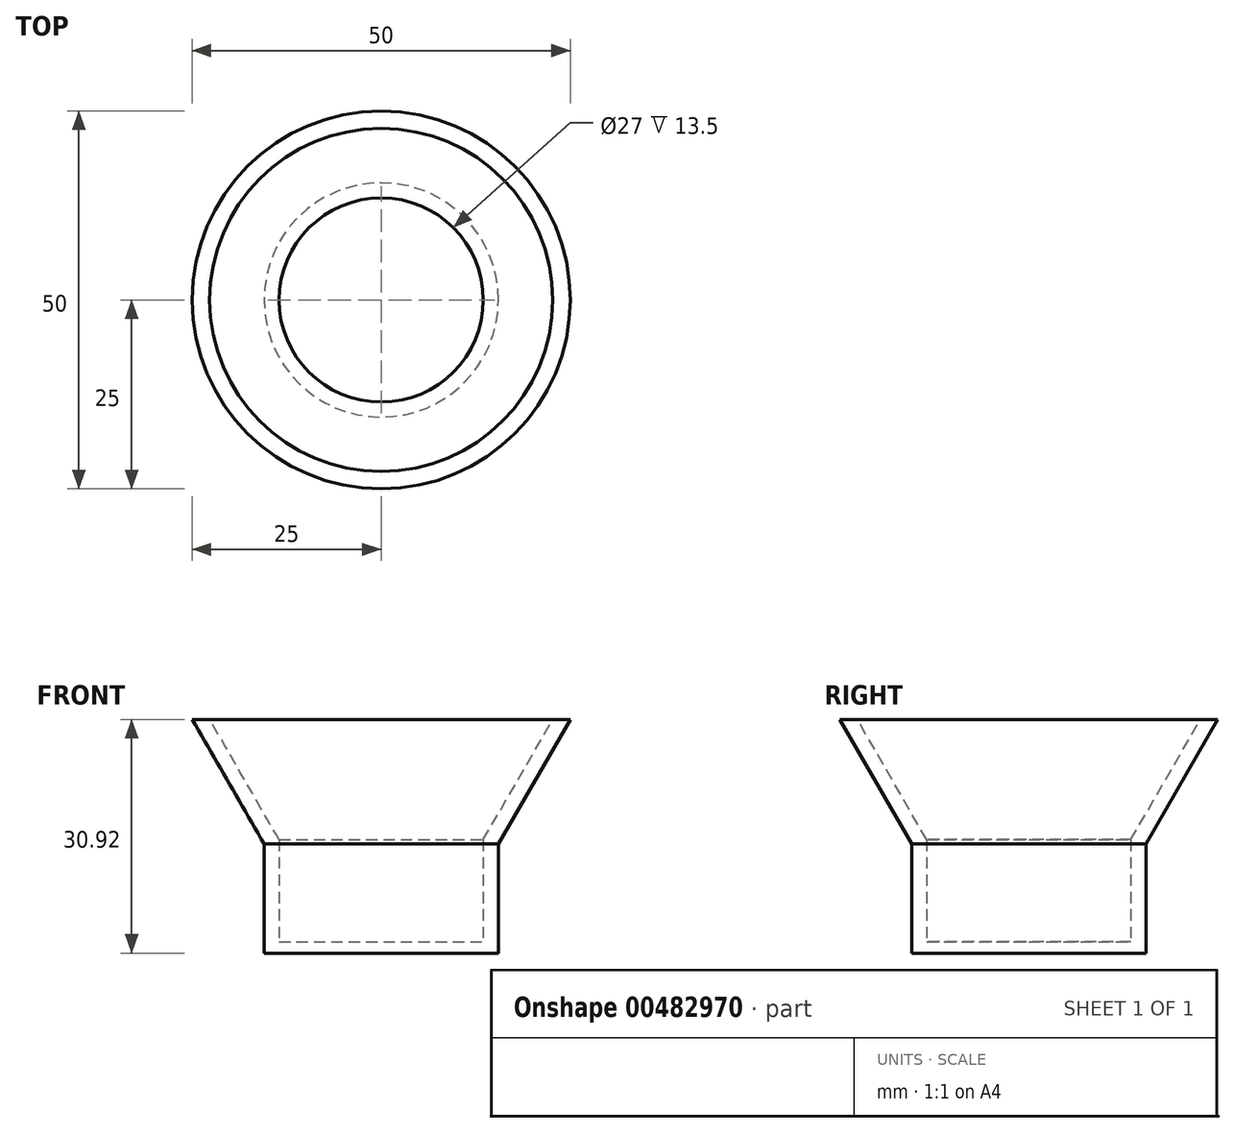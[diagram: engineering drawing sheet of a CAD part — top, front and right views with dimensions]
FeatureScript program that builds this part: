
annotation { "Feature Type Name" : "Feature", "Feature Type Description" : "" }
export const myFeature = defineFeature(function(context is Context, id is Id, definition is map)
    precondition{}
    {
        {
            var Q0;
            Q0=qCreatedBy(makeId("Front.planeOp"),FACE);
            var sketch = newSketch(context, id + "F0", { "sketchPlane" : qUnion([Q0])});
            skLineSegment(sketch, "E0", {"start": v(0, 0) * mm, "end": v(0, 42.36) * mm, "construction": true});
            skLineSegment(sketch, "E1", {"start": v(13.5, 0) * mm, "end": v(13.5, 15) * mm});
            skLineSegment(sketch, "E2", {"start": v(13.5, 15) * mm, "end": v(22.7, 30.92) * mm});
            skLineSegment(sketch, "E3", {"start": v(22.7, 30.92) * mm, "end": v(25, 30.92) * mm});
            skLineSegment(sketch, "E4", {"start": v(25, 30.92) * mm, "end": v(15.5, 14.46) * mm});
            skLineSegment(sketch, "E5", {"start": v(15.5, 14.46) * mm, "end": v(15.5, 0) * mm});
            skLineSegment(sketch, "E6", {"start": v(15.5, 0) * mm, "end": v(13.5, 0) * mm});
            skLineSegment(sketch, "E7.MirrorCS", {"start": v(-22.7, 30.92) * mm, "end": v(-25, 30.92) * mm});
            skLineSegment(sketch, "E8.MirrorCS", {"start": v(-15.5, 0) * mm, "end": v(-13.5, 0) * mm});
            skLineSegment(sketch, "E9.MirrorCS", {"start": v(-13.5, 15) * mm, "end": v(-22.7, 30.92) * mm});
            skLineSegment(sketch, "E10.MirrorCS", {"start": v(-25, 30.92) * mm, "end": v(-15.5, 14.46) * mm});
            skLineSegment(sketch, "E11.MirrorCS", {"start": v(-13.5, 0) * mm, "end": v(-13.5, 15) * mm});
            skLineSegment(sketch, "E12.MirrorCS", {"start": v(-15.5, 14.46) * mm, "end": v(-15.5, 0) * mm});
            skLineSegment(sketch, "E13", {"start": v(13.5, 0) * mm, "end": v(0, 0) * mm});
            skLineSegment(sketch, "E14", {"start": v(0, 1.5) * mm, "end": v(13.5, 1.5) * mm});
            skLineSegment(sketch, "E15", {"start": v(0, 1.5) * mm, "end": v(0, 0) * mm});
            skSolve(sketch);
        }
        {
            var Q0;
            {var subQ0=sQuery(id+"F0.wireOp",EDGE,"E2");Q0=makeQuery(id+"F0.imprint","IMPRINT",FACE,{"disambiguationData":[TD([[makeQuery(id+"F0.imprint","IMPRINT",EDGE,{"derivedFrom":subQ0}),-1.0]])]});}
            var Q1;
            {var subQ0=sQuery(id+"F0.wireOp",EDGE,"E13");Q1=makeQuery(id+"F0.imprint","IMPRINT",FACE,{"disambiguationData":[TD([[makeQuery(id+"F0.imprint","IMPRINT",EDGE,{"derivedFrom":subQ0}),-1.0]])]});}
            var Q2;
            Q2=sQuery(id+"F0.wireOp",EDGE,"E0");
            revolve(context, id + "F1", {"entities" : qUnion([Q0, Q1]), "axis" : qUnion([Q2]), "revolveType" : RevolveType.FULL});
        }
    });
